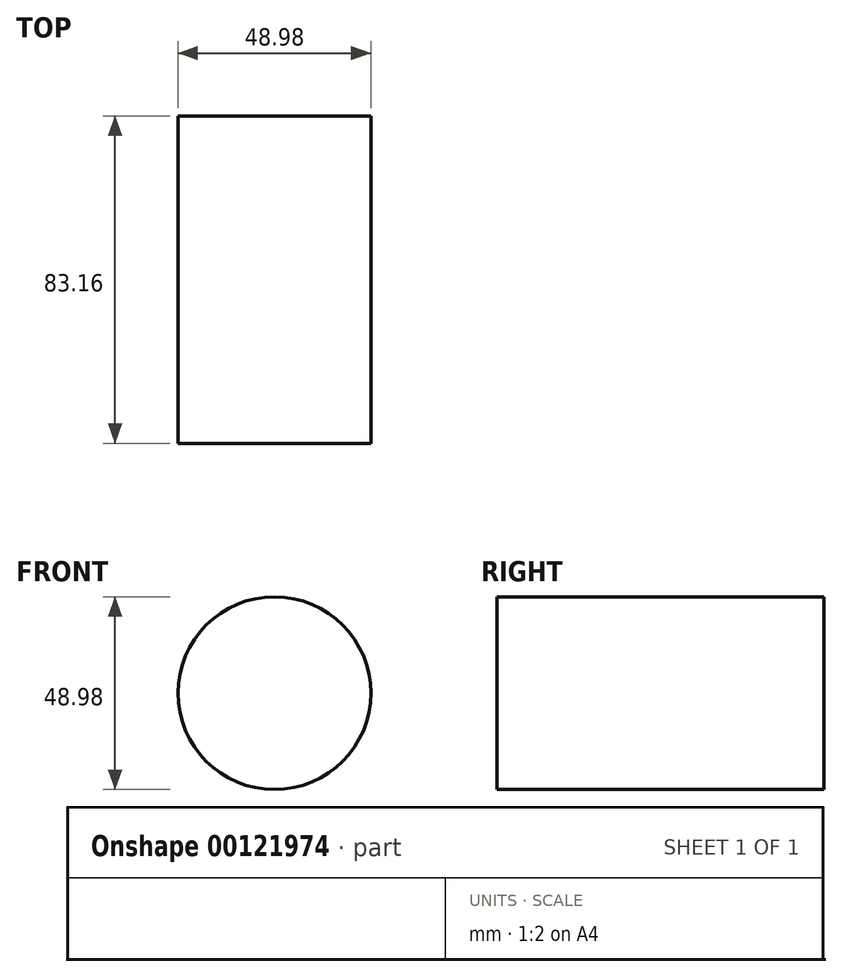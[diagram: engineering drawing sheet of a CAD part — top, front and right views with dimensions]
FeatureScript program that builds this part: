
annotation { "Feature Type Name" : "Feature", "Feature Type Description" : "" }
export const myFeature = defineFeature(function(context is Context, id is Id, definition is map)
    precondition{}
    {
        {
            var Q0;
            Q0=qCreatedBy(makeId("Front.planeOp"),FACE);
            var sketch = newSketch(context, id + "F0", { "sketchPlane" : qUnion([Q0])});
            skCircle(sketch, "E0", {"center": v(0, 0) * mm, "radius": 24.5 * mm});
            skSolve(sketch);
        }
        {
            var Q0;
            Q0=makeQuery(id+"F0.imprint","IMPRINT",FACE,{"disambiguationData":[TD([[makeQuery(id+"F0.imprint","IMPRINT",EDGE,{"derivedFrom":sQuery(id+"F0.wireOp",EDGE,"E0")}),1.0]])]});
            extrude(context, id + "F1", {"entities" : qUnion([Q0]), "depth" : 83.16 * mm});
        }
    });
